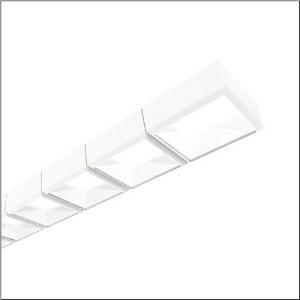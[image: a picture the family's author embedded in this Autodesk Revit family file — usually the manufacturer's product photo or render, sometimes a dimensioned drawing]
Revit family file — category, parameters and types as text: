
# Revit family: scriptus_r__11_5mz212d04wa_64be
name_source: partatom
category: Lighting Fixtures
units: mm (PartAtom-declared; Revit-internal decimal feet)

## family parameters
Cut with Voids When Loaded = No
Host = Face
Light Source = No
Part Type = Normal
Room Calculation Point = No
Round Connector Dimension = Use Diameter
Shared = No

## types (1)
- Scriptus® 11 (1 x LED 4000K / CRI = 80 (unbekannt), 2410 lm, 4000K)
    Apparent Load = 35 VA
    CIE Flux Codes = 82 95 99 100 100
    Color Rendering = 80
    Color Temperature = 4000K
    Default Elevation = 1800 mm
    Description = Scriptus® 11, office luminaire, primary optical cover: lenses, CAT 2 (L<= 3000cd/m²), light emission: direct distribution, primary light characteristic: symmetric, installation type: surface-mounted, LED rated luminous flux: 4.810 lm, light colour: 840, colour temperature: 4000K, control gear: ECG DALI, with terminal, 5-pole, mains connection: 230V, AC, 50Hz, rated input power: 35W, housing, luminaire housing, of aluminium, traffic white (RAL 9016), length: 1.658 mm, width: 114 mm, height: 57mm, protection rating (complete): IP20, insulation class (complete): insulation class I (protective earthing), certification: CE, ENEC, VDE, protection symbol: F, permissible ambient temperature for indoor applications: 0..+35°C, standard: EN 50419, packaging unit: 1 piece
    Height = 57 mm
    Lamp = 1 x LED 4000K / CRI >= 80 (unbekannt)
    Lamp Light Flux = 2410 lm
    Lamp count = 1
    Length = 1658 mm
    Luminous efficacy = 139 lm/W
    Manufacturer = Siteco
    ModVariant = No
    Model = 5MZ212D04WA
    Mounting Place = Ceiling
    Mounting Type = Surface mounted
    Number of Poles = 1
    OnlyDefault = Yes
    Power Factor = 1
    Product Name = Scriptus® 11
    Product group = office luminaire | ceiling mounted
    ProductGroupID = 302
    Protection Class = Protection class I
    Protection Degree = IP 20
    RLX_Detail_Level = 1
    RlxData = <blob elided: 29521 chars, md5=70557e32>
    Socket = socket
    Standby Power = 0 W
    System Light Flux = 4820 lm
    System Power = 35 W
    Type Comments = Product without accessories
    Type Image = l_1004833.jpg
    URL = http://relux.com
    VarID = ---
    Voltage = 0 V
    Weight = 0.00 kg
    Width = 114 mm

## geometry (parser evidence)
native form markers: Blend x4, Sweep x13
no freeform markers — native parametric forms only
